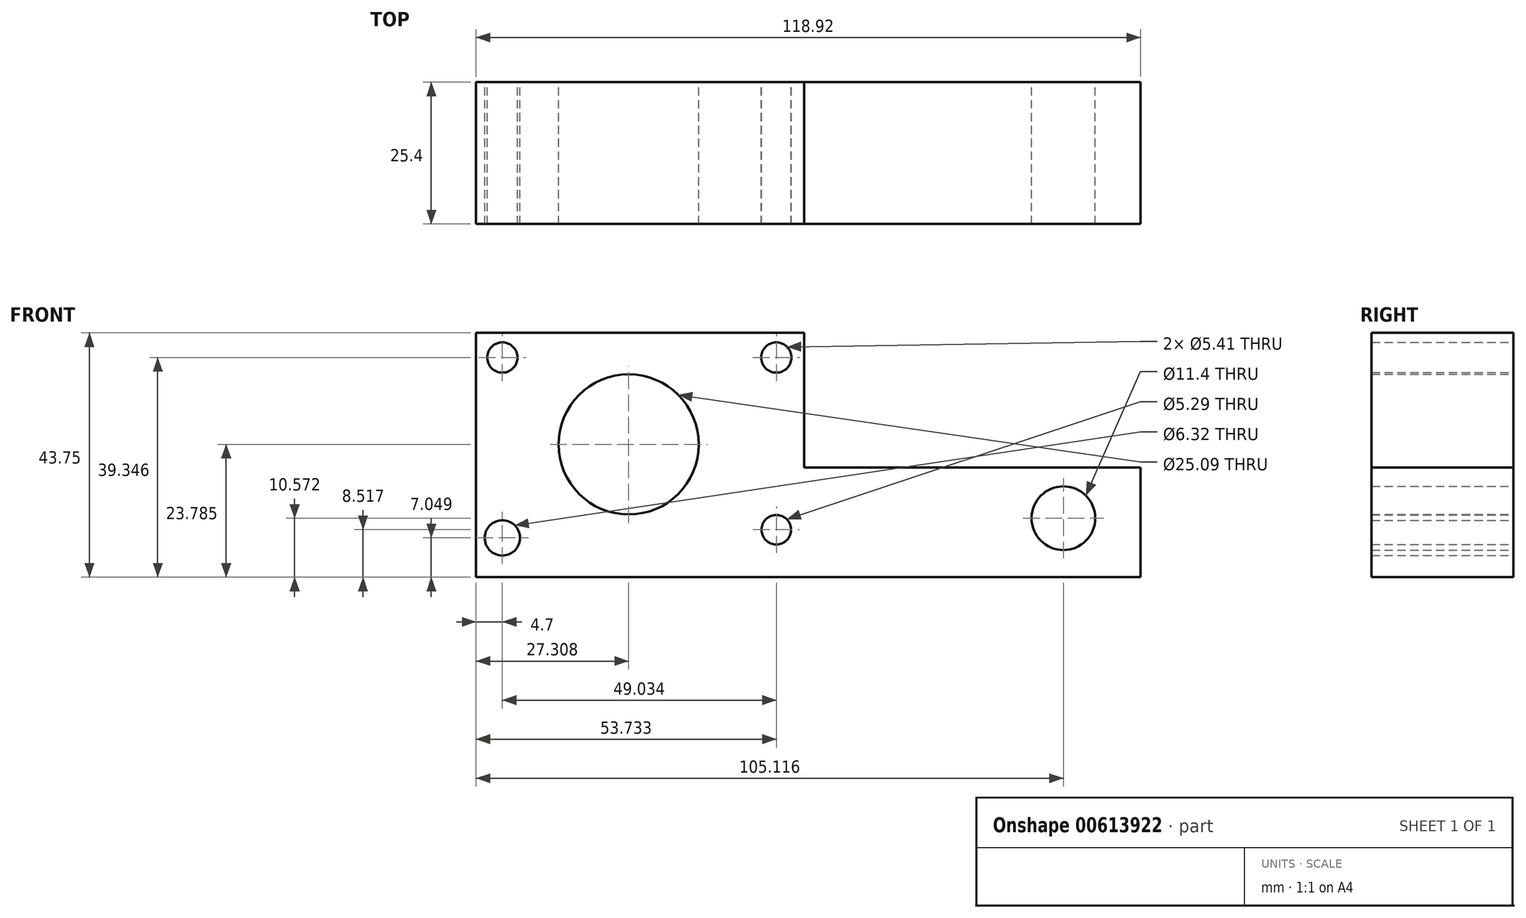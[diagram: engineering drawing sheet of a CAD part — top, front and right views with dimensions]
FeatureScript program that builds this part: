
annotation { "Feature Type Name" : "Feature", "Feature Type Description" : "" }
export const myFeature = defineFeature(function(context is Context, id is Id, definition is map)
    precondition{}
    {
        {
            var Q0;
            Q0=qCreatedBy(makeId("Front.planeOp"),FACE);
            var sketch = newSketch(context, id + "F0", { "sketchPlane" : qUnion([Q0])});
            skLineSegment(sketch, "E0", {"start": v(-67.68, 56.08) * mm, "end": v(-8.96, 56.08) * mm});
            skLineSegment(sketch, "E1", {"start": v(-8.96, 56.08) * mm, "end": v(-8.96, 32) * mm});
            skLineSegment(sketch, "E2", {"start": v(-8.96, 32) * mm, "end": v(51.24, 32) * mm});
            skLineSegment(sketch, "E3", {"start": v(51.24, 32) * mm, "end": v(51.24, 12.33) * mm});
            skLineSegment(sketch, "E4", {"start": v(51.24, 12.33) * mm, "end": v(-67.68, 12.33) * mm});
            skLineSegment(sketch, "E5", {"start": v(-67.68, 12.33) * mm, "end": v(-67.68, 56.08) * mm});
            skCircle(sketch, "E6", {"center": v(-62.98, 51.68) * mm, "radius": 2.7 * mm});
            skCircle(sketch, "E7", {"center": v(-13.95, 51.68) * mm, "radius": 2.7 * mm});
            skCircle(sketch, "E8", {"center": v(-62.98, 19.38) * mm, "radius": 3.16 * mm});
            skCircle(sketch, "E9", {"center": v(-13.95, 20.85) * mm, "radius": 2.64 * mm});
            skCircle(sketch, "E10", {"center": v(37.44, 22.9) * mm, "radius": 5.7 * mm});
            skCircle(sketch, "E11", {"center": v(-40.37, 36.11) * mm, "radius": 12.54 * mm});
            skSolve(sketch);
        }
        {
            var Q0;
            Q0 = qSketchRegion(id + "F0", true);
            extrude(context, id + "F1", {"entities" : qUnion([Q0]), "depth" : 25.4 * mm, "offsetDistance" : 25.4 * mm});
        }
    });
